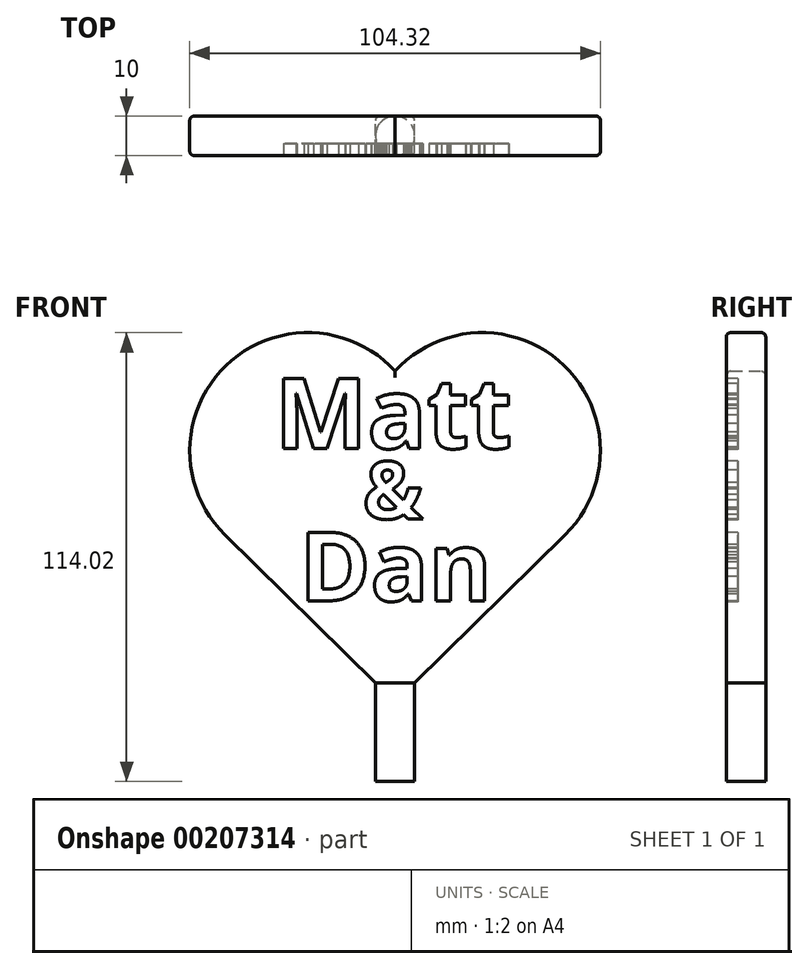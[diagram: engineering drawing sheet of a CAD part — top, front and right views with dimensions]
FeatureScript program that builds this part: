
annotation { "Feature Type Name" : "Feature", "Feature Type Description" : "" }
export const myFeature = defineFeature(function(context is Context, id is Id, definition is map)
    precondition{}
    {
        {
            var Q0;
            Q0=qCreatedBy(makeId("Front.planeOp"),FACE);
            var sketch = newSketch(context, id + "F0", { "sketchPlane" : qUnion([Q0])});
            skLineSegment(sketch, "E0", {"start": v(0, 0) * mm, "end": v(-43.21, 42.55) * mm});
            skArc(sketch, "E1", {"start": v(0, 84.16) * mm, "mid": v(-42.97, 85.55) * mm, "end": v(-43.21, 42.55) * mm});
            skArc(sketch, "E2.MirrorCS", {"start": v(0, 84.16) * mm, "mid": v(42.97, 85.55) * mm, "end": v(43.21, 42.55) * mm});
            skLineSegment(sketch, "E3.MirrorCS", {"start": v(0, 0) * mm, "end": v(43.21, 42.55) * mm});
            skLineSegment(sketch, "E4", {"start": v(-5, 4.92) * mm, "end": v(5, 4.92) * mm});
            skSolve(sketch);
        }
        {
            var Q0;
            {var subQ3=sQuery(id+"F0.wireOp",EDGE,"E1");Q0=makeQuery(id+"F0.imprint","IMPRINT",FACE,{"disambiguationData":[TD([[makeQuery(id+"F0.imprint","IMPRINT",EDGE,{"derivedFrom":subQ3}),1.0]])]});}
            extrude(context, id + "F1", {"entities" : qUnion([Q0]), "depth" : 10 * mm});
        }
        {
            var Q0;
            Q0=makeQuery(id+"F1.opExtrude","CAP_EDGE",EDGE,{"disambiguationData":[OSD([sQuery(id+"F0.wireOp",EDGE,"E1")])],"isStart":false});
            var Q1;
            Q1=makeQuery(id+"F1.opExtrude","CAP_EDGE",EDGE,{"disambiguationData":[OSD([sQuery(id+"F0.wireOp",EDGE,"E2.MirrorCS")])],"isStart":false});
            var Q2;
            Q2=makeQuery(id+"F1.opExtrude","CAP_EDGE",EDGE,{"disambiguationData":[OSD([sQuery(id+"F0.wireOp",EDGE,"E0")])],"isStart":false});
            var Q3;
            Q3=makeQuery(id+"F1.opExtrude","CAP_EDGE",EDGE,{"disambiguationData":[OSD([sQuery(id+"F0.wireOp",EDGE,"E3.MirrorCS")])],"isStart":false});
            var Q4;
            Q4=makeQuery(id+"F1.opExtrude","CAP_EDGE",EDGE,{"disambiguationData":[OSD([sQuery(id+"F0.wireOp",EDGE,"E0")])],"isStart":true});
            var Q5;
            Q5=makeQuery(id+"F1.opExtrude","CAP_EDGE",EDGE,{"disambiguationData":[OSD([sQuery(id+"F0.wireOp",EDGE,"E1")])],"isStart":true});
            var Q6;
            Q6=makeQuery(id+"F1.opExtrude","CAP_EDGE",EDGE,{"disambiguationData":[OSD([sQuery(id+"F0.wireOp",EDGE,"E2.MirrorCS")])],"isStart":true});
            var Q7;
            Q7=makeQuery(id+"F1.opExtrude","CAP_EDGE",EDGE,{"disambiguationData":[OSD([sQuery(id+"F0.wireOp",EDGE,"E3.MirrorCS")])],"isStart":true});
            fillet(context, id + "F2", {"entities" : qUnion([Q0, Q1, Q2, Q3, Q4, Q5, Q6, Q7]), "radius" : 1.1 * mm, "tangentPropagation" : true, "allowEdgeOverflow" : false});
        }
        {
            var Q0;
            Q0=makeQuery(id+"F1.opExtrude","SWEPT_FACE",FACE,{"disambiguationData":[OSD([sQuery(id+"F0.wireOp",EDGE,"E4")])]});
            var sketch = newSketch(context, id + "F3", { "sketchPlane" : qUnion([Q0])});
            skCircle(sketch, "E5", {"center": v(0, 5) * mm, "radius": 5 * mm});
            skPoint(sketch, "E5.centerSnap0", {"position": v(5, 5) * mm});
            skSolve(sketch);
        }
        {
            var Q0;
            Q0 = qSketchRegion(id + "F3", true);
            extrude(context, id + "F4", {"entities" : qUnion([Q0]), "operationType" : NewBodyOperationType.ADD, "depth" : 25 * mm});
        }
        {
            var Q0;
            Q0=makeQuery(id+"F1.opExtrude","CAP_FACE",FACE,{"disambiguationData":[OSD([sQuery(id+"F0.wireOp",EDGE,"E0"),sQuery(id+"F0.wireOp",EDGE,"E1"),sQuery(id+"F0.wireOp",EDGE,"E2.MirrorCS"),sQuery(id+"F0.wireOp",EDGE,"E3.MirrorCS"),sQuery(id+"F0.wireOp",EDGE,"E4")])],"isStart":false});
            var sketch = newSketch(context, id + "F5", { "sketchPlane" : qUnion([Q0])});
            skText(sketch, "E6", { "text": "Matt", "fontName": "OpenSans-Bold.ttf"});
            skText(sketch, "E7", { "text": "Dan", "fontName": "OpenSans-Bold.ttf"});
            skText(sketch, "E8", { "text": "&", "fontName": "OpenSans-Bold.ttf"});
            const initialGuessF5  = {"E6": [-0.03053, 0.06453, 1, 0, 0.01796], "E7": [-0.02432, 0.02576, 1, 0, 0.01759], "E8": [-0.00819, 0.0466, 1, 0, 0.01468]};
            skSetInitialGuess(sketch, initialGuessF5);
            skSolve(sketch);
        }
        {
            var Q0;
            Q0 = qSketchRegion(id + "F5", true);
            extrude(context, id + "F6", {"entities" : qUnion([Q0]), "operationType" : NewBodyOperationType.REMOVE, "oppositeDirection" : true, "depth" : 3 * mm});
        }
    });
